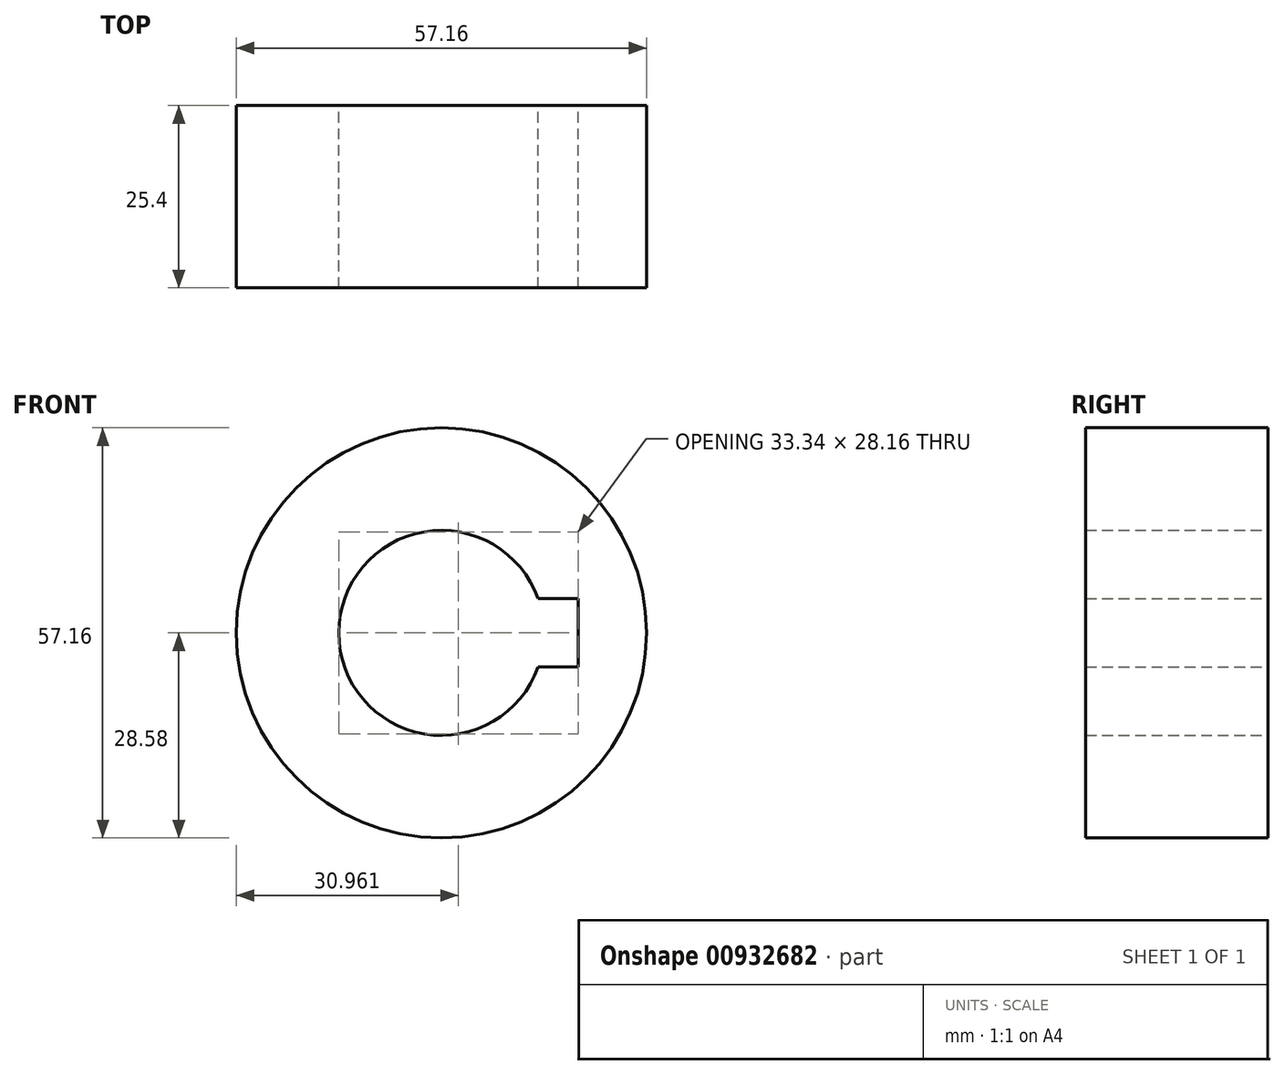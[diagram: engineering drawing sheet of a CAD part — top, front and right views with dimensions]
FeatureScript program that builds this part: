
annotation { "Feature Type Name" : "Feature", "Feature Type Description" : "" }
export const myFeature = defineFeature(function(context is Context, id is Id, definition is map)
    precondition{}
    {
        {
            var Q0;
            Q0=qCreatedBy(makeId("Front.planeOp"),FACE);
            var sketch = newSketch(context, id + "F0", { "sketchPlane" : qUnion([Q0])});
            skCircle(sketch, "E0", {"center": v(0, 0) * mm, "radius": 28.58 * mm});
            skCircle(sketch, "E1", {"center": v(76.2, 0) * mm, "radius": 19.05 * mm});
            skLineSegment(sketch, "E2", {"start": v(3.57, 28.35) * mm, "end": v(78.58, 18.9) * mm});
            skLineSegment(sketch, "E3", {"start": v(3.57, -28.35) * mm, "end": v(78.58, -18.9) * mm});
            skCircle(sketch, "E4", {"center": v(0, 0) * mm, "radius": 14.29 * mm});
            skCircle(sketch, "E5", {"center": v(76.2, 0) * mm, "radius": 14.29 * mm});
            skLineSegment(sketch, "E6.bottom", {"start": v(-19.05, 4.76) * mm, "end": v(19.05, 4.76) * mm});
            skLineSegment(sketch, "E6.top", {"start": v(-19.05, -4.76) * mm, "end": v(19.05, -4.76) * mm});
            skLineSegment(sketch, "E6.left", {"start": v(-19.05, 4.76) * mm, "end": v(-19.05, -4.76) * mm});
            skLineSegment(sketch, "E6.right", {"start": v(19.05, 4.76) * mm, "end": v(19.05, -4.76) * mm});
            skSolve(sketch);
        }
        {
            var Q0;
            {var subQ7=sQuery(id+"F0.wireOp",EDGE,"E6.left");Q0=makeQuery(id+"F0.imprint","IMPRINT",FACE,{"disambiguationData":[TD([[makeQuery(id+"F0.imprint","IMPRINT",EDGE,{"derivedFrom":subQ7}),-1.0]])]});}
            var Q1;
            {var subQ5=sQuery(id+"F0.wireOp",EDGE,"E6.left");Q1=makeQuery(id+"F0.imprint","IMPRINT",FACE,{"disambiguationData":[TD([[makeQuery(id+"F0.imprint","IMPRINT",EDGE,{"derivedFrom":subQ5}),1.0]])]});}
            extrude(context, id + "F1", {"entities" : qUnion([Q0, Q1]), "depth" : 25.4 * mm, "offsetDistance" : 25.4 * mm});
        }
    });
